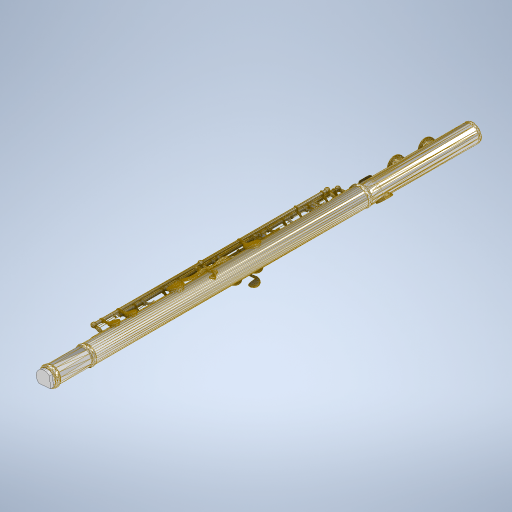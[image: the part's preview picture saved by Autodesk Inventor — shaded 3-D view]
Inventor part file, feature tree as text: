
AUTODESK INVENTOR PART (.ipt)
format: ipt  version: 2024 (Build 280153000, 153)  size: 60,340,224 bytes
history: native  units: in
note: dims shown in document units (in); Inventor stores cm internally (conversion verified against a paired STEP export)
features: other x3, plane x3, extrude x2, projected_geometry x1
ambient origin geometry x8: Origin, YZ Plane, XZ Plane, XY Plane, X Axis, Y Axis, Z Axis, Center Point
bodies: Solid1 (feature_tree)
feature tree (9):
  other  "resto_flauta"
  plane  "Work Plane1"
  extrude  "Extrusion1"  Depth=0.1in TaperAngle=0.0deg
  plane  "Work Plane3"
  extrude  "Extrusion2"  Depth=0.1in TaperAngle=0.0deg
  plane  "Work Plane4"
  projected_geometry  "Projected Loop1"
  other  "MeshFeature1"
  other  "Srf1"
